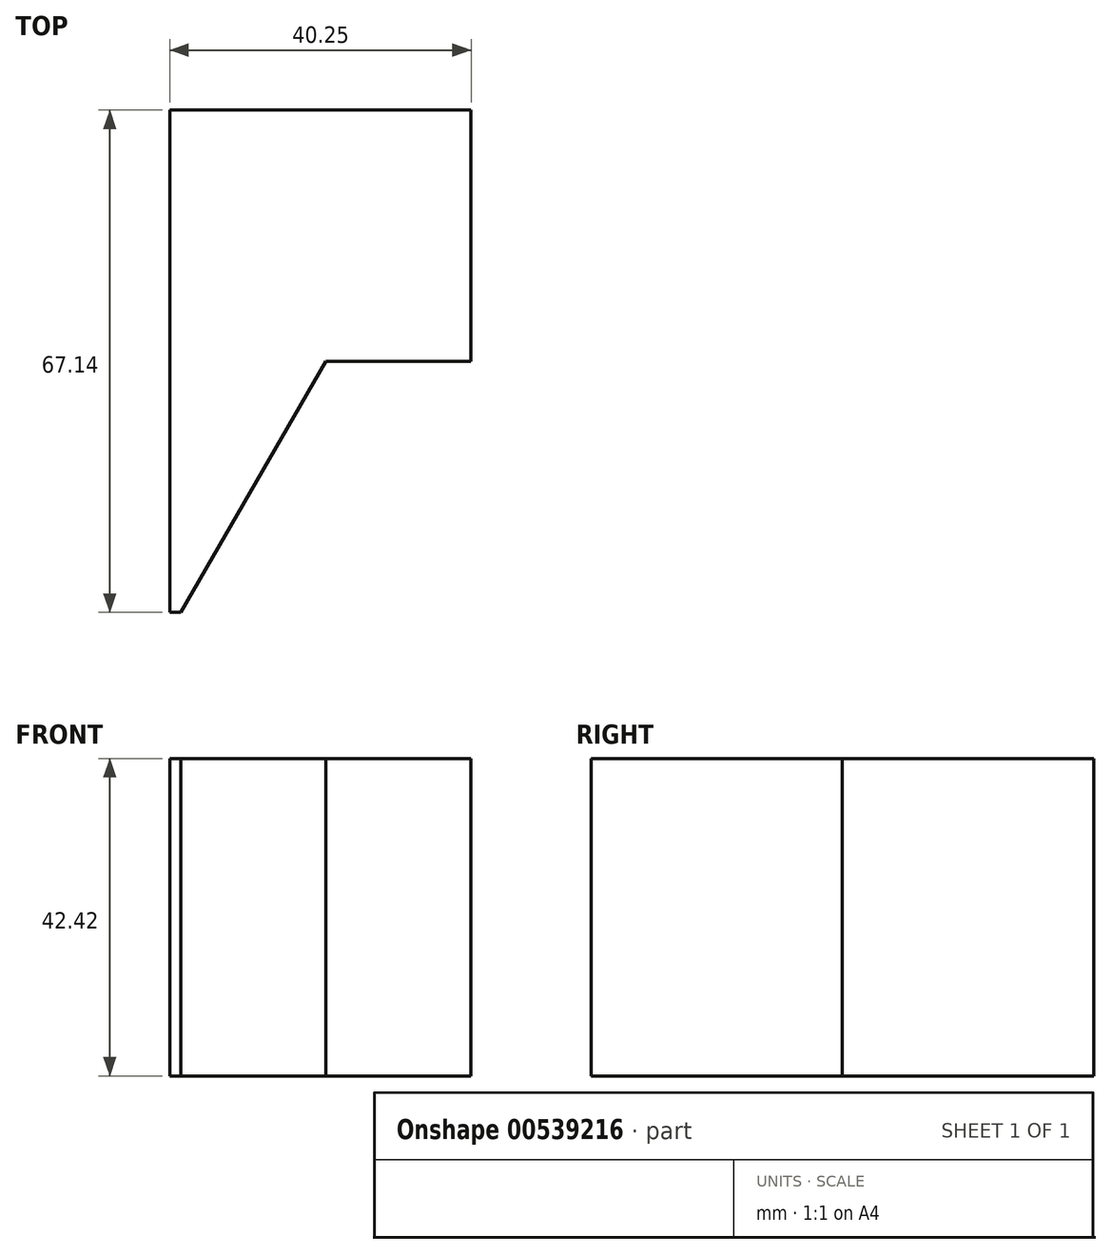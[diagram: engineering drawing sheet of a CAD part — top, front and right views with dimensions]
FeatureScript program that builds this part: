
annotation { "Feature Type Name" : "Feature", "Feature Type Description" : "" }
export const myFeature = defineFeature(function(context is Context, id is Id, definition is map)
    precondition{}
    {
        {
            var Q0;
            Q0=qCreatedBy(makeId("Top.planeOp"),FACE);
            var sketch = newSketch(context, id + "F0", { "sketchPlane" : qUnion([Q0])});
            skLineSegment(sketch, "E0.bottom", {"start": v(40.25, 0) * mm, "end": v(0, 0) * mm});
            skLineSegment(sketch, "E0.top", {"start": v(40.25, -67.14) * mm, "end": v(0, -67.14) * mm});
            skLineSegment(sketch, "E0.left", {"start": v(40.25, 0) * mm, "end": v(40.25, -67.14) * mm});
            skLineSegment(sketch, "E0.right", {"start": v(0, 0) * mm, "end": v(0, -67.14) * mm});
            skSolve(sketch);
        }
        {
            var Q0;
            Q0 = qSketchRegion(id + "F0", true);
            extrude(context, id + "F1", {"entities" : qUnion([Q0]), "depth" : 42.42 * mm, "offsetDistance" : 25.4 * mm});
        }
        {
            var Q0;
            Q0=makeQuery(id+"F1.opExtrude","CAP_FACE",FACE,{"disambiguationData":[OSD([sQuery(id+"F0.wireOp",EDGE,"E0.bottom"),sQuery(id+"F0.wireOp",EDGE,"E0.top"),sQuery(id+"F0.wireOp",EDGE,"E0.left"),sQuery(id+"F0.wireOp",EDGE,"E0.right")])],"isStart":false});
            var sketch = newSketch(context, id + "F2", { "sketchPlane" : qUnion([Q0])});
            skCircle(sketch, "E1.cCircle", {"center": v(40.25, -67.14) * mm, "radius": 33.57 * mm, "construction": true});
            skLineSegment(sketch, "E1.0", {"start": v(20.87, -33.57) * mm, "end": v(59.63, -33.57) * mm});
            skLineSegment(sketch, "E1.1", {"start": v(59.63, -33.57) * mm, "end": v(79, -67.14) * mm});
            skLineSegment(sketch, "E1.2", {"start": v(79, -67.14) * mm, "end": v(59.63, -100.7) * mm});
            skLineSegment(sketch, "E1.3", {"start": v(59.63, -100.7) * mm, "end": v(20.87, -100.7) * mm});
            skLineSegment(sketch, "E1.4", {"start": v(20.87, -100.7) * mm, "end": v(1.49, -67.14) * mm});
            skLineSegment(sketch, "E1.5", {"start": v(1.49, -67.14) * mm, "end": v(20.87, -33.57) * mm});
            skPoint(sketch, "E1.0.midPoint", {"position": v(40.25, -33.57) * mm});
            skSolve(sketch);
        }
        {
            var Q0;
            Q0 = qSketchRegion(id + "F2", true);
            extrude(context, id + "F3", {"entities" : qUnion([Q0]), "operationType" : NewBodyOperationType.REMOVE, "oppositeDirection" : true, "depth" : 68.1 * mm, "offsetDistance" : 25.4 * mm});
        }
    });
